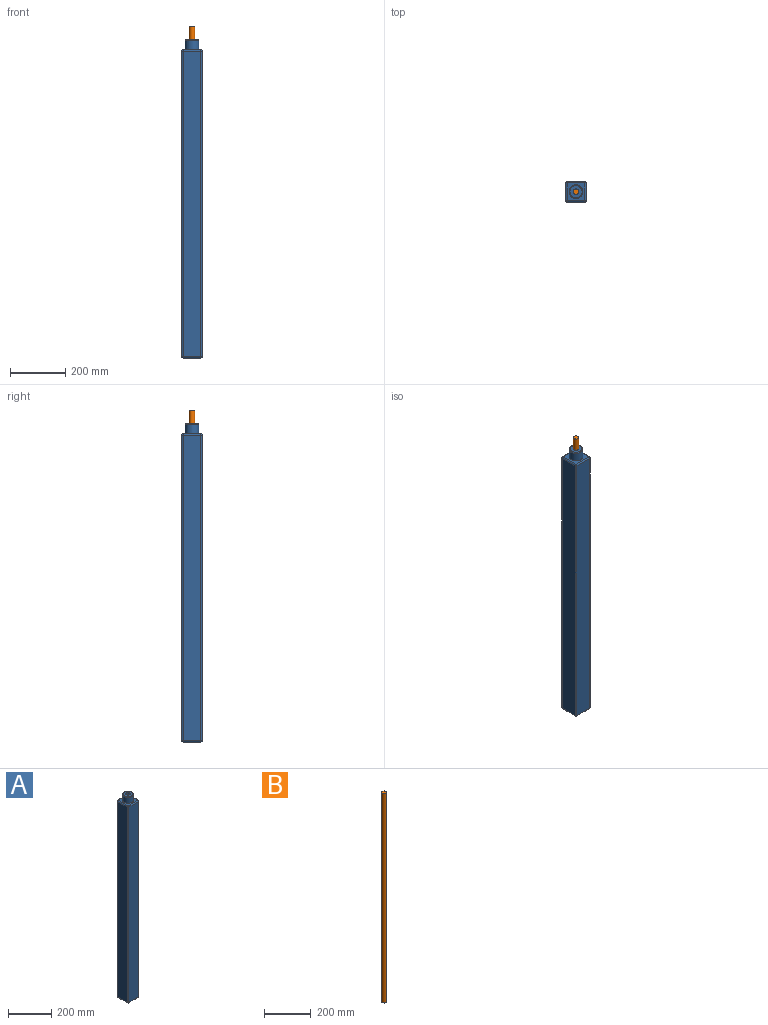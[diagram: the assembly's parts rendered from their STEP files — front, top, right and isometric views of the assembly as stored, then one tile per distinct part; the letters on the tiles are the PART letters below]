
ASSEMBLY  parts=2 mates=1
PART A: 31 faces, bbox 75x75x1157 mm
  f0: cylinder r=5mm len=1111mm, axis (0,0,-1), area 8725.8mm2, adj f1,f7,f20,f27
  f1: plane 1111x65mm, normal (0,-1,0), area 72215mm2, adj f0,f2,f22,f25
  f2: cylinder r=5mm len=1111mm, axis (0,0,-1), area 8725.8mm2, adj f1,f3,f21,f23
  f3: plane 1111x65mm, normal (1,0,0), area 72215mm2, adj f2,f4,f19,f24
  f4: cylinder r=5mm len=1111mm, axis (0,0,-1), area 8725.8mm2, adj f3,f5,f17,f26
  f5: plane 1111x65mm, normal (0,1,0), area 72215mm2, adj f4,f6,f15,f28
  f6: cylinder r=5mm len=1111mm, axis (0,0,-1), area 8725.8mm2, adj f5,f7,f16,f30
  f7: plane 1111x65mm, normal (-1,0,0), area 72215mm2, adj f0,f6,f18,f29
  f8: plane 65x65mm, normal (0,0,1), area 2261.5mm2, adj f10,f15,f18,f19,f22
  f9: plane 65x65mm, normal (0,0,-1), area 4225mm2, adj f24,f25,f28,f29
  f10: cylinder r=25mm len=50mm, axis (0,0,-1), area 5183.6mm2, adj f8,f12
  f11: plane 44x44mm, normal (0,0,1), area 1206.4mm2, adj f12,f13
  f12: torus R=22mm, axis (0,0,1), area 707.9mm2, adj f10,f11
  f13: cylinder r=10mm len=1100mm, axis (0,0,1), area 69115mm2, adj f11,f14
  f14: plane 20x20mm, normal (0,0,1), area 314.2mm2, adj f13
  f15: cylinder r=5mm len=65mm, axis (1,0,0), area 510.5mm2, adj f5,f8,f16,f17
  f16: sphere r=5mm, area 39.3mm2, adj f6,f15,f18
  f17: sphere r=5mm, area 39.3mm2, adj f4,f15,f19
  f18: cylinder r=5mm len=65mm, axis (0,1,0), area 510.5mm2, adj f7,f8,f16,f20
  f19: cylinder r=5mm len=65mm, axis (0,-1,0), area 510.5mm2, adj f3,f8,f17,f21
  f20: sphere r=5mm, area 39.3mm2, adj f0,f18,f22
  f21: sphere r=5mm, area 39.3mm2, adj f2,f19,f22
  f22: cylinder r=5mm len=65mm, axis (-1,0,0), area 510.5mm2, adj f1,f8,f20,f21
  f23: sphere r=5mm, area 39.3mm2, adj f2,f24,f25
  f24: cylinder r=5mm len=65mm, axis (0,1,0), area 510.5mm2, adj f3,f9,f23,f26
  f25: cylinder r=5mm len=65mm, axis (1,0,0), area 510.5mm2, adj f1,f9,f23,f27
  f26: sphere r=5mm, area 39.3mm2, adj f4,f24,f28
  f27: sphere r=5mm, area 39.3mm2, adj f0,f25,f29
  f28: cylinder r=5mm len=65mm, axis (-1,0,0), area 510.5mm2, adj f5,f9,f26,f30
  f29: cylinder r=5mm len=65mm, axis (0,-1,0), area 510.5mm2, adj f7,f9,f27,f30
  f30: sphere r=5mm, area 39.3mm2, adj f6,f28,f29
PART B: 3 faces, bbox 20x20x1100 mm
  f0: cylinder r=10mm len=1100mm, axis (0,0,-1), area 69115mm2, adj f1,f2
  f1: plane 20x20mm, normal (0,0,1), area 314.2mm2, adj f0
  f2: plane 20x20mm, normal (0,0,-1), area 314.2mm2, adj f0
PLACE A t=(-405.9,51.56,-149.64)mm fixed
PLACE B rot(axis=(1,0,0),180deg) t=(-405.9,51.56,1057.36)mm
MATE slider B.f0 <-> A.f10  axis (0,0,1) through (-405.9,51.56,1057.36)mm
